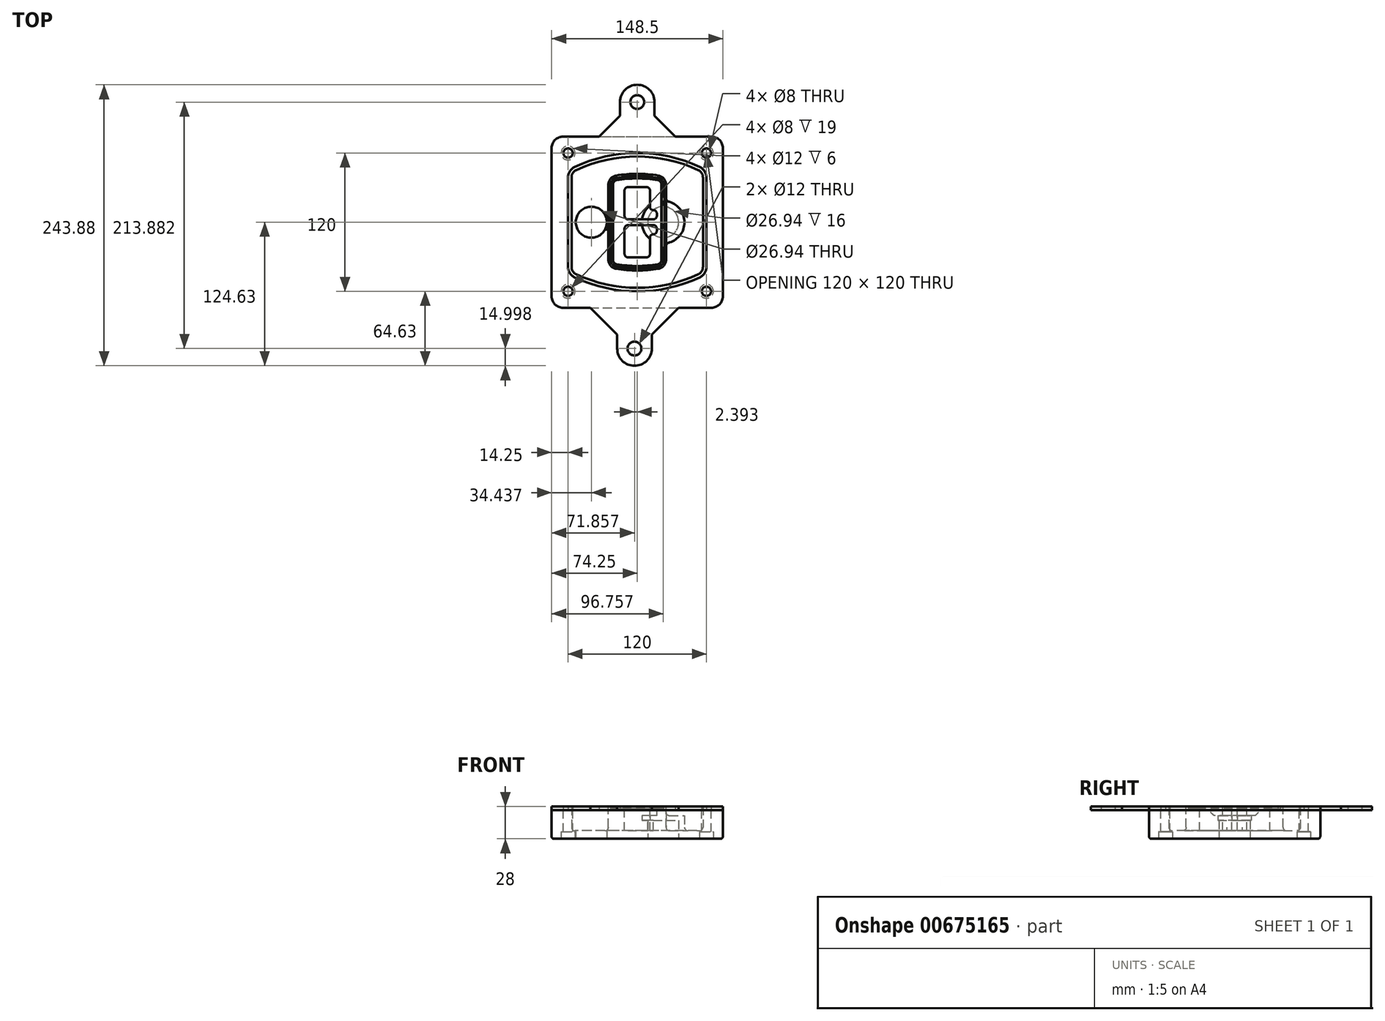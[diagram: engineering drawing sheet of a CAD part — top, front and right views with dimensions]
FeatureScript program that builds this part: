
annotation { "Feature Type Name" : "Feature", "Feature Type Description" : "" }
export const myFeature = defineFeature(function(context is Context, id is Id, definition is map)
    precondition{}
    {
        {
            var Q0;
            Q0=qCreatedBy(makeId("Top.planeOp"),FACE);
            var sketch = newSketch(context, id + "F0", { "sketchPlane" : qUnion([Q0])});
            skPoint(sketch, "E0.rect.middle", {"position": v(0, 0) * mm});
            skLineSegment(sketch, "E1.bottom", {"start": v(-64.25, -74.25) * mm, "end": v(64.25, -74.25) * mm});
            skLineSegment(sketch, "E1.top", {"start": v(-64.25, 74.25) * mm, "end": v(64.25, 74.25) * mm});
            skLineSegment(sketch, "E1.left", {"start": v(-74.25, -64.25) * mm, "end": v(-74.25, 64.25) * mm});
            skLineSegment(sketch, "E1.right", {"start": v(74.25, -64.25) * mm, "end": v(74.25, 64.25) * mm});
            skLineSegment(sketch, "E2", {"start": v(-74.25, 74.25) * mm, "end": v(74.25, -74.25) * mm, "construction": true});
            skLineSegment(sketch, "E3", {"start": v(74.25, 74.25) * mm, "end": v(-74.25, -74.25) * mm, "construction": true});
            skCircle(sketch, "E4", {"center": v(-60, 60) * mm, "radius": 4 * mm});
            skCircle(sketch, "E5", {"center": v(60, 60) * mm, "radius": 4 * mm});
            skCircle(sketch, "E6", {"center": v(60, -60) * mm, "radius": 4 * mm});
            skCircle(sketch, "E7", {"center": v(-60, -60) * mm, "radius": 4 * mm});
            skLineSegment(sketch, "E8", {"start": v(-60, 60) * mm, "end": v(60, 60) * mm, "construction": true});
            skLineSegment(sketch, "E9", {"start": v(60, 60) * mm, "end": v(60, -60) * mm, "construction": true});
            skLineSegment(sketch, "E10", {"start": v(60, -60) * mm, "end": v(-60, -60) * mm, "construction": true});
            skLineSegment(sketch, "E11", {"start": v(-60, -60) * mm, "end": v(-60, 60) * mm, "construction": true});
            skLineSegment(sketch, "E12", {"start": v(-60, 38.83) * mm, "end": v(-60, -38.83) * mm});
            skLineSegment(sketch, "E13", {"start": v(60, 38.83) * mm, "end": v(60, -38.83) * mm});
            skArc(sketch, "E14", {"start": v(54.26, 47.88) * mm, "mid": v(0, 60) * mm, "end": v(-54.26, 47.88) * mm});
            skArc(sketch, "E15", {"start": v(-54.26, -47.88) * mm, "mid": v(0, -60) * mm, "end": v(54.26, -47.88) * mm});
            skLineSegment(sketch, "E16", {"start": v(-60, 0) * mm, "end": v(60, 0) * mm, "construction": true});
            skPoint(sketch, "E17.visualSharp", {"position": v(-60, -45) * mm});
            skArc(sketch, "E17.filletArc", {"start": v(-60, -38.83) * mm, "mid": v(-58.44, -44.2) * mm, "end": v(-54.26, -47.88) * mm});
            skPoint(sketch, "E18.visualSharp", {"position": v(-60, 45) * mm});
            skArc(sketch, "E18.filletArc", {"start": v(-54.26, 47.88) * mm, "mid": v(-58.44, 44.2) * mm, "end": v(-60, 38.83) * mm});
            skPoint(sketch, "E19.visualSharp", {"position": v(60, 45) * mm});
            skArc(sketch, "E19.filletArc", {"start": v(60, 38.83) * mm, "mid": v(58.44, 44.2) * mm, "end": v(54.26, 47.88) * mm});
            skPoint(sketch, "E20.visualSharp", {"position": v(60, -45) * mm});
            skArc(sketch, "E20.filletArc", {"start": v(54.26, -47.88) * mm, "mid": v(58.44, -44.2) * mm, "end": v(60, -38.83) * mm});
            skPoint(sketch, "E21.visualSharp", {"position": v(-74.25, 74.25) * mm});
            skArc(sketch, "E21.filletArc", {"start": v(-64.25, 74.25) * mm, "mid": v(-71.32, 71.32) * mm, "end": v(-74.25, 64.25) * mm});
            skPoint(sketch, "E22.visualSharp", {"position": v(74.25, 74.25) * mm});
            skArc(sketch, "E22.filletArc", {"start": v(74.25, 64.25) * mm, "mid": v(71.32, 71.32) * mm, "end": v(64.25, 74.25) * mm});
            skPoint(sketch, "E23.visualSharp", {"position": v(74.25, -74.25) * mm});
            skArc(sketch, "E23.filletArc", {"start": v(64.25, -74.25) * mm, "mid": v(71.32, -71.32) * mm, "end": v(74.25, -64.25) * mm});
            skPoint(sketch, "E24.visualSharp", {"position": v(-74.25, -74.25) * mm});
            skArc(sketch, "E24.filletArc", {"start": v(-74.25, -64.25) * mm, "mid": v(-71.32, -71.32) * mm, "end": v(-64.25, -74.25) * mm});
            skArc(sketch, "E25.0", {"start": v(57, 38.83) * mm, "mid": v(55.9, 42.58) * mm, "end": v(52.98, 45.17) * mm});
            skLineSegment(sketch, "E25.1", {"start": v(57, 38.83) * mm, "end": v(57, -38.83) * mm});
            skArc(sketch, "E25.2", {"start": v(52.98, -45.17) * mm, "mid": v(55.9, -42.58) * mm, "end": v(57, -38.83) * mm});
            skArc(sketch, "E25.3", {"start": v(-52.98, -45.17) * mm, "mid": v(0, -57) * mm, "end": v(52.98, -45.17) * mm});
            skArc(sketch, "E25.4", {"start": v(-57, -38.83) * mm, "mid": v(-55.9, -42.58) * mm, "end": v(-52.98, -45.17) * mm});
            skArc(sketch, "E25.5", {"start": v(52.98, 45.17) * mm, "mid": v(0, 57) * mm, "end": v(-52.98, 45.17) * mm});
            skLineSegment(sketch, "E25.6", {"start": v(-57, 38.83) * mm, "end": v(-57, -38.83) * mm});
            skArc(sketch, "E25.7", {"start": v(-52.98, 45.17) * mm, "mid": v(-55.9, 42.58) * mm, "end": v(-57, 38.83) * mm});
            skArc(sketch, "E26.0", {"start": v(-55.96, 51.5) * mm, "mid": v(-61.82, 46.33) * mm, "end": v(-64, 38.83) * mm});
            skArc(sketch, "E26.1", {"start": v(55.96, 51.5) * mm, "mid": v(0, 64) * mm, "end": v(-55.96, 51.5) * mm});
            skArc(sketch, "E26.2", {"start": v(64, 38.83) * mm, "mid": v(61.82, 46.33) * mm, "end": v(55.96, 51.5) * mm});
            skLineSegment(sketch, "E26.3", {"start": v(64, 38.83) * mm, "end": v(64, -38.83) * mm});
            skArc(sketch, "E26.4", {"start": v(55.96, -51.5) * mm, "mid": v(61.82, -46.33) * mm, "end": v(64, -38.83) * mm});
            skLineSegment(sketch, "E26.5", {"start": v(-64, 38.83) * mm, "end": v(-64, -38.83) * mm});
            skArc(sketch, "E26.6", {"start": v(-55.96, -51.5) * mm, "mid": v(0, -64) * mm, "end": v(55.96, -51.5) * mm});
            skArc(sketch, "E26.7", {"start": v(-64, -38.83) * mm, "mid": v(-61.82, -46.33) * mm, "end": v(-55.96, -51.5) * mm});
            skPoint(sketch, "E27.startSnap0", {"position": v(0, 74.25) * mm});
            skCircle(sketch, "E28", {"center": v(0, 104.25) * mm, "radius": 6 * mm});
            skArc(sketch, "E29", {"start": v(-15, 104.25) * mm, "mid": v(0, 119.25) * mm, "end": v(15, 104.25) * mm});
            skLineSegment(sketch, "E30", {"start": v(-15, 104.25) * mm, "end": v(-15, 92.25) * mm});
            skLineSegment(sketch, "E31", {"start": v(15, 104.25) * mm, "end": v(15, 92.25) * mm});
            skLineSegment(sketch, "E32", {"start": v(-15, 92.25) * mm, "end": v(-33, 74.25) * mm});
            skLineSegment(sketch, "E33", {"start": v(15, 92.25) * mm, "end": v(33, 74.25) * mm});
            skCircle(sketch, "E34", {"center": v(-2.4, -109.63) * mm, "radius": 6 * mm});
            skArc(sketch, "E35", {"start": v(-17.4, -109.63) * mm, "mid": v(-2.4, -124.63) * mm, "end": v(12.6, -109.63) * mm});
            skLineSegment(sketch, "E36", {"start": v(12.6, -109.63) * mm, "end": v(12.6, -97.63) * mm});
            skLineSegment(sketch, "E37", {"start": v(-17.4, -109.63) * mm, "end": v(-17.4, -97.63) * mm});
            skLineSegment(sketch, "E38", {"start": v(12.6, -97.63) * mm, "end": v(35.99, -74.25) * mm});
            skLineSegment(sketch, "E39", {"start": v(-17.4, -97.63) * mm, "end": v(-40.77, -74.25) * mm});
            skSolve(sketch);
        }
        {
            var Q0;
            Q0=makeQuery(id+"F0.imprint","IMPRINT",FACE,{"disambiguationData":[TD([[makeQuery(id+"F0.imprint","IMPRINT",EDGE,{"derivedFrom":sQuery(id+"F0.wireOp",EDGE,"E1.bottom")}),1.0]])]});
            var Q1;
            Q1=makeQuery(id+"F0.imprint","IMPRINT",FACE,{"disambiguationData":[TD([[makeQuery(id+"F0.imprint","IMPRINT",EDGE,{"derivedFrom":sQuery(id+"F0.wireOp",EDGE,"E12")}),1.0]])]});
            var Q2;
            Q2=makeQuery(id+"F0.imprint","IMPRINT",FACE,{"disambiguationData":[TD([[makeQuery(id+"F0.imprint","IMPRINT",EDGE,{"derivedFrom":sQuery(id+"F0.wireOp",EDGE,"E25.0")}),1.0]])]});
            var Q3;
            Q3=makeQuery(id+"F0.imprint","IMPRINT",FACE,{"disambiguationData":[TD([[makeQuery(id+"F0.imprint","IMPRINT",EDGE,{"derivedFrom":sQuery(id+"F0.wireOp",EDGE,"E12")}),-1.0]])]});
            extrude(context, id + "F1", {"entities" : qUnion([Q0, Q1, Q2, Q3]), "oppositeDirection" : true, "depth" : 25 * mm});
        }
        {
            var Q0;
            Q0=makeQuery(id+"F0.imprint","IMPRINT",FACE,{"disambiguationData":[TD([[makeQuery(id+"F0.imprint","IMPRINT",EDGE,{"derivedFrom":sQuery(id+"F0.wireOp",EDGE,"E12")}),1.0]])]});
            extrude(context, id + "F2", {"entities" : qUnion([Q0]), "operationType" : NewBodyOperationType.ADD, "depth" : 3 * mm});
        }
        {
            var Q0;
            Q0=makeQuery(id+"F0.imprint","IMPRINT",FACE,{"disambiguationData":[TD([[makeQuery(id+"F0.imprint","IMPRINT",EDGE,{"derivedFrom":sQuery(id+"F0.wireOp",EDGE,"E25.0")}),1.0]])]});
            extrude(context, id + "F3", {"entities" : qUnion([Q0]), "operationType" : NewBodyOperationType.REMOVE, "oppositeDirection" : true, "depth" : 18 * mm});
        }
        {
            var Q0;
            Q0=makeQuery(id+"F2.opExtrude","CAP_FACE",FACE,{"disambiguationData":[OSD([sQuery(id+"F0.wireOp",EDGE,"E12"),sQuery(id+"F0.wireOp",EDGE,"E13"),sQuery(id+"F0.wireOp",EDGE,"E14"),sQuery(id+"F0.wireOp",EDGE,"E15"),sQuery(id+"F0.wireOp",EDGE,"E17.filletArc"),sQuery(id+"F0.wireOp",EDGE,"E18.filletArc"),sQuery(id+"F0.wireOp",EDGE,"E19.filletArc"),sQuery(id+"F0.wireOp",EDGE,"E20.filletArc"),sQuery(id+"F0.wireOp",EDGE,"E25.0"),sQuery(id+"F0.wireOp",EDGE,"E25.1"),sQuery(id+"F0.wireOp",EDGE,"E25.2"),sQuery(id+"F0.wireOp",EDGE,"E25.3"),sQuery(id+"F0.wireOp",EDGE,"E25.4"),sQuery(id+"F0.wireOp",EDGE,"E25.5"),sQuery(id+"F0.wireOp",EDGE,"E25.6"),sQuery(id+"F0.wireOp",EDGE,"E25.7")])],"isStart":false});
            var sketch = newSketch(context, id + "F4", { "sketchPlane" : qUnion([Q0])});
            skArc(sketch, "E40.0", {"start": v(-18.34, -40.45) * mm, "mid": v(0, -42) * mm, "end": v(18.34, -40.45) * mm});
            skArc(sketch, "E41.0", {"start": v(18.34, 40.45) * mm, "mid": v(0, 42) * mm, "end": v(-18.34, 40.45) * mm});
            skLineSegment(sketch, "E42", {"start": v(-25, 32.57) * mm, "end": v(-25, -32.57) * mm});
            skLineSegment(sketch, "E43", {"start": v(25, 32.57) * mm, "end": v(25, -32.57) * mm});
            skLineSegment(sketch, "E44", {"start": v(-25, 39.1) * mm, "end": v(25, 39.1) * mm, "construction": true});
            skLineSegment(sketch, "E45", {"start": v(-25, -39.1) * mm, "end": v(25, -39.1) * mm, "construction": true});
            skPoint(sketch, "E46.visualSharp", {"position": v(-25, 39.1) * mm});
            skArc(sketch, "E46.filletArc", {"start": v(-18.34, 40.45) * mm, "mid": v(-23.11, 37.73) * mm, "end": v(-25, 32.57) * mm});
            skPoint(sketch, "E47.visualSharp", {"position": v(25, 39.1) * mm});
            skArc(sketch, "E47.filletArc", {"start": v(25, 32.57) * mm, "mid": v(23.11, 37.73) * mm, "end": v(18.34, 40.45) * mm});
            skPoint(sketch, "E48.visualSharp", {"position": v(25, -39.1) * mm});
            skArc(sketch, "E48.filletArc", {"start": v(18.34, -40.45) * mm, "mid": v(23.11, -37.73) * mm, "end": v(25, -32.57) * mm});
            skPoint(sketch, "E49.visualSharp", {"position": v(-25, -39.1) * mm});
            skArc(sketch, "E49.filletArc", {"start": v(-25, -32.57) * mm, "mid": v(-23.11, -37.73) * mm, "end": v(-18.34, -40.45) * mm});
            skArc(sketch, "E50.0", {"start": v(52.98, 45.17) * mm, "mid": v(0, 57) * mm, "end": v(-52.98, 45.17) * mm});
            skArc(sketch, "E50.1", {"start": v(-52.98, 45.17) * mm, "mid": v(-55.9, 42.58) * mm, "end": v(-57, 38.83) * mm});
            skLineSegment(sketch, "E50.2", {"start": v(-57, 38.83) * mm, "end": v(-57, -38.83) * mm});
            skArc(sketch, "E50.3", {"start": v(-57, -38.83) * mm, "mid": v(-55.9, -42.58) * mm, "end": v(-52.98, -45.17) * mm});
            skArc(sketch, "E50.4", {"start": v(-52.98, -45.17) * mm, "mid": v(0, -57) * mm, "end": v(52.98, -45.17) * mm});
            skArc(sketch, "E50.5", {"start": v(52.98, -45.17) * mm, "mid": v(55.9, -42.58) * mm, "end": v(57, -38.83) * mm});
            skLineSegment(sketch, "E50.6", {"start": v(57, 38.83) * mm, "end": v(57, -38.83) * mm});
            skArc(sketch, "E50.7", {"start": v(57, 38.83) * mm, "mid": v(55.9, 42.58) * mm, "end": v(52.98, 45.17) * mm});
            skLineSegment(sketch, "E51.0", {"start": v(23, 32.57) * mm, "end": v(23, -32.57) * mm});
            skArc(sketch, "E51.1", {"start": v(18, -38.48) * mm, "mid": v(21.58, -36.44) * mm, "end": v(23, -32.57) * mm});
            skArc(sketch, "E51.2", {"start": v(-18, -38.48) * mm, "mid": v(0, -40) * mm, "end": v(18, -38.48) * mm});
            skArc(sketch, "E51.3", {"start": v(-23, -32.57) * mm, "mid": v(-21.58, -36.44) * mm, "end": v(-18, -38.48) * mm});
            skLineSegment(sketch, "E51.4", {"start": v(-23, 32.57) * mm, "end": v(-23, -32.57) * mm});
            skArc(sketch, "E51.5", {"start": v(23, 32.57) * mm, "mid": v(21.58, 36.44) * mm, "end": v(18, 38.48) * mm});
            skArc(sketch, "E51.6", {"start": v(-18, 38.48) * mm, "mid": v(-21.58, 36.44) * mm, "end": v(-23, 32.57) * mm});
            skArc(sketch, "E51.7", {"start": v(18, 38.48) * mm, "mid": v(0, 40) * mm, "end": v(-18, 38.48) * mm});
            skArc(sketch, "E52.0", {"start": v(21, 32.57) * mm, "mid": v(20.06, 35.15) * mm, "end": v(17.67, 36.5) * mm});
            skLineSegment(sketch, "E52.1", {"start": v(21, 32.57) * mm, "end": v(21, -32.57) * mm});
            skArc(sketch, "E52.2", {"start": v(17.67, -36.5) * mm, "mid": v(20.06, -35.15) * mm, "end": v(21, -32.57) * mm});
            skArc(sketch, "E52.3", {"start": v(-17.67, -36.5) * mm, "mid": v(0, -38) * mm, "end": v(17.67, -36.5) * mm});
            skArc(sketch, "E52.4", {"start": v(-21, -32.57) * mm, "mid": v(-20.06, -35.15) * mm, "end": v(-17.67, -36.5) * mm});
            skArc(sketch, "E52.5", {"start": v(17.67, 36.5) * mm, "mid": v(0, 38) * mm, "end": v(-17.67, 36.5) * mm});
            skLineSegment(sketch, "E52.6", {"start": v(-21, 32.57) * mm, "end": v(-21, -32.57) * mm});
            skArc(sketch, "E52.7", {"start": v(-17.67, 36.5) * mm, "mid": v(-20.06, 35.15) * mm, "end": v(-21, 32.57) * mm});
            skLineSegment(sketch, "E53", {"start": v(-25, 0) * mm, "end": v(25, 0) * mm, "construction": true});
            skLineSegment(sketch, "E54", {"start": v(-11, 5.5) * mm, "end": v(-11, 27.5) * mm});
            skLineSegment(sketch, "E55", {"start": v(-8, 30.5) * mm, "end": v(8, 30.5) * mm});
            skLineSegment(sketch, "E56", {"start": v(11, 27.5) * mm, "end": v(11, 13.5) * mm});
            skLineSegment(sketch, "E57", {"start": v(14, 10.5) * mm, "end": v(14, 10.5) * mm});
            skLineSegment(sketch, "E58", {"start": v(17, 7.5) * mm, "end": v(17, 5.5) * mm});
            skLineSegment(sketch, "E59", {"start": v(14, 2.5) * mm, "end": v(-8, 2.5) * mm});
            skPoint(sketch, "E60.visualSharp", {"position": v(-11, 30.5) * mm});
            skArc(sketch, "E60.filletArc", {"start": v(-8, 30.5) * mm, "mid": v(-10.12, 29.62) * mm, "end": v(-11, 27.5) * mm});
            skPoint(sketch, "E61.visualSharp", {"position": v(11, 30.5) * mm});
            skArc(sketch, "E61.filletArc", {"start": v(11, 27.5) * mm, "mid": v(10.12, 29.62) * mm, "end": v(8, 30.5) * mm});
            skPoint(sketch, "E62.visualSharp", {"position": v(11, 10.5) * mm});
            skArc(sketch, "E62.filletArc", {"start": v(11, 13.5) * mm, "mid": v(11.88, 11.38) * mm, "end": v(14, 10.5) * mm});
            skPoint(sketch, "E63.visualSharp", {"position": v(17, 10.5) * mm});
            skArc(sketch, "E63.filletArc", {"start": v(17, 7.5) * mm, "mid": v(16.12, 9.62) * mm, "end": v(14, 10.5) * mm});
            skPoint(sketch, "E64.visualSharp", {"position": v(17, 2.5) * mm});
            skArc(sketch, "E64.filletArc", {"start": v(14, 2.5) * mm, "mid": v(16.12, 3.38) * mm, "end": v(17, 5.5) * mm});
            skPoint(sketch, "E65.visualSharp", {"position": v(-11, 2.5) * mm});
            skArc(sketch, "E65.filletArc", {"start": v(-11, 5.5) * mm, "mid": v(-10.12, 3.38) * mm, "end": v(-8, 2.5) * mm});
            skLineSegment(sketch, "E66.0.MirrorCS", {"start": v(14, -2.5) * mm, "end": v(-8, -2.5) * mm});
            skArc(sketch, "E67.0.MirrorCS", {"start": v(-11, -5.5) * mm, "mid": v(-10.12, -3.38) * mm, "end": v(-8, -2.5) * mm});
            skLineSegment(sketch, "E68.0.MirrorCS", {"start": v(-11, -5.5) * mm, "end": v(-11, -27.5) * mm});
            skArc(sketch, "E69.0.MirrorCS", {"start": v(-8, -30.5) * mm, "mid": v(-10.12, -29.62) * mm, "end": v(-11, -27.5) * mm});
            skLineSegment(sketch, "E70.0.MirrorCS", {"start": v(-8, -30.5) * mm, "end": v(8, -30.5) * mm});
            skArc(sketch, "E71.0.MirrorCS", {"start": v(11, -27.5) * mm, "mid": v(10.12, -29.62) * mm, "end": v(8, -30.5) * mm});
            skLineSegment(sketch, "E72.0.MirrorCS", {"start": v(11, -27.5) * mm, "end": v(11, -13.5) * mm});
            skArc(sketch, "E73.0.MirrorCS", {"start": v(11, -13.5) * mm, "mid": v(11.88, -11.38) * mm, "end": v(14, -10.5) * mm});
            skArc(sketch, "E74.0.MirrorCS", {"start": v(17, -7.5) * mm, "mid": v(16.12, -9.62) * mm, "end": v(14, -10.5) * mm});
            skLineSegment(sketch, "E75.0.MirrorCS", {"start": v(17, -7.5) * mm, "end": v(17, -5.5) * mm});
            skArc(sketch, "E76.0.MirrorCS", {"start": v(14, -2.5) * mm, "mid": v(16.12, -3.38) * mm, "end": v(17, -5.5) * mm});
            skSolve(sketch);
        }
        {
            var Q0;
            Q0=makeQuery(id+"F4.imprint","IMPRINT",FACE,{"disambiguationData":[TD([[makeQuery(id+"F4.imprint","IMPRINT",EDGE,{"derivedFrom":sQuery(id+"F4.wireOp",EDGE,"E40.0")}),1.0]])]});
            var Q1;
            Q1=makeQuery(id+"F4.imprint","IMPRINT",FACE,{"disambiguationData":[TD([[makeQuery(id+"F4.imprint","IMPRINT",EDGE,{"derivedFrom":sQuery(id+"F4.wireOp",EDGE,"E51.0")}),-1.0]])]});
            var Q2;
            Q2=makeQuery(id+"F4.imprint","IMPRINT",FACE,{"disambiguationData":[TD([[makeQuery(id+"F4.imprint","IMPRINT",EDGE,{"derivedFrom":sQuery(id+"F4.wireOp",EDGE,"E52.0")}),1.0]])]});
            extrude(context, id + "F5", {"entities" : qUnion([Q0, Q1, Q2]), "operationType" : NewBodyOperationType.ADD, "endBound" : BoundingType.UP_TO_NEXT, "oppositeDirection" : true, "depth" : 25 * mm});
        }
        {
            var Q0;
            Q0=makeQuery(id+"F4.imprint","IMPRINT",FACE,{"disambiguationData":[TD([[makeQuery(id+"F4.imprint","IMPRINT",EDGE,{"derivedFrom":sQuery(id+"F4.wireOp",EDGE,"E51.0")}),-1.0]])]});
            extrude(context, id + "F6", {"entities" : qUnion([Q0]), "operationType" : NewBodyOperationType.REMOVE, "oppositeDirection" : true, "depth" : 2 * mm});
        }
        {
            var Q0;
            Q0=makeQuery(id+"F1.opExtrude","CAP_FACE",FACE,{"disambiguationData":[OSD([sQuery(id+"F0.wireOp",EDGE,"E1.bottom"),sQuery(id+"F0.wireOp",EDGE,"E1.top"),sQuery(id+"F0.wireOp",EDGE,"E1.left"),sQuery(id+"F0.wireOp",EDGE,"E1.right"),sQuery(id+"F0.wireOp",EDGE,"E4"),sQuery(id+"F0.wireOp",EDGE,"E5"),sQuery(id+"F0.wireOp",EDGE,"E6"),sQuery(id+"F0.wireOp",EDGE,"E7"),sQuery(id+"F0.wireOp",EDGE,"E21.filletArc"),sQuery(id+"F0.wireOp",EDGE,"E22.filletArc"),sQuery(id+"F0.wireOp",EDGE,"E23.filletArc"),sQuery(id+"F0.wireOp",EDGE,"E24.filletArc")])],"isStart":false});
            var sketch = newSketch(context, id + "F7", { "sketchPlane" : qUnion([Q0])});
            skCircle(sketch, "E77", {"center": v(22.5, 0) * mm, "radius": 13.47 * mm});
            skCircle(sketch, "E78", {"center": v(-39.81, 0) * mm, "radius": 13.47 * mm});
            skLineSegment(sketch, "E79", {"start": v(74.25, 0) * mm, "end": v(-74.25, 0) * mm});
            skCircle(sketch, "E80", {"center": v(22.5, 0) * mm, "radius": 18.47 * mm});
            skCircle(sketch, "E81", {"center": v(60, -60) * mm, "radius": 6 * mm});
            skCircle(sketch, "E82", {"center": v(-60, -60) * mm, "radius": 6 * mm});
            skCircle(sketch, "E83", {"center": v(-60, 60) * mm, "radius": 6 * mm});
            skCircle(sketch, "E84", {"center": v(60, 60) * mm, "radius": 6 * mm});
            skSolve(sketch);
        }
        {
            var Q0;
            {var subQ1=sQuery(id+"F7.wireOp",EDGE,"E79");var subQ4=sQuery(id+"F7.wireOp",EDGE,"E77");var subQ6=makeQuery(id+"F7.imprint","INTERSECT",VERTEX,{"disambiguationData":[OD(0.0)],"derivedFrom":[subQ4,subQ1]});Q0=makeQuery(id+"F7.imprint","IMPRINT",FACE,{"disambiguationData":[TD([[makeQuery(id+"F7.imprint","IMPRINT",EDGE,{"disambiguationData":[TD([[subQ6,-1.0]])],"derivedFrom":subQ4}),-1.0]])]});}
            var Q1;
            {var subQ0=sQuery(id+"F7.wireOp",EDGE,"E79");var subQ1=sQuery(id+"F7.wireOp",EDGE,"E77");var subQ3=makeQuery(id+"F7.imprint","INTERSECT",VERTEX,{"disambiguationData":[OD(0.0)],"derivedFrom":[subQ1,subQ0]});Q1=makeQuery(id+"F7.imprint","IMPRINT",FACE,{"disambiguationData":[TD([[makeQuery(id+"F7.imprint","IMPRINT",EDGE,{"disambiguationData":[TD([[subQ3,-1.0]])],"derivedFrom":subQ1}),1.0]])]});}
            var Q2;
            {var subQ0=sQuery(id+"F7.wireOp",EDGE,"E79");var subQ1=sQuery(id+"F7.wireOp",EDGE,"E77");var subQ3=makeQuery(id+"F7.imprint","INTERSECT",VERTEX,{"disambiguationData":[OD(0.0)],"derivedFrom":[subQ1,subQ0]});Q2=makeQuery(id+"F7.imprint","IMPRINT",FACE,{"disambiguationData":[TD([[makeQuery(id+"F7.imprint","IMPRINT",EDGE,{"disambiguationData":[TD([[subQ3,1.0]])],"derivedFrom":subQ1}),1.0]])]});}
            var Q3;
            {var subQ1=sQuery(id+"F7.wireOp",EDGE,"E79");var subQ4=sQuery(id+"F7.wireOp",EDGE,"E77");var subQ6=makeQuery(id+"F7.imprint","INTERSECT",VERTEX,{"disambiguationData":[OD(0.0)],"derivedFrom":[subQ4,subQ1]});Q3=makeQuery(id+"F7.imprint","IMPRINT",FACE,{"disambiguationData":[TD([[makeQuery(id+"F7.imprint","IMPRINT",EDGE,{"disambiguationData":[TD([[subQ6,1.0]])],"derivedFrom":subQ4}),-1.0]])]});}
            extrude(context, id + "F8", {"entities" : qUnion([Q0, Q1, Q2, Q3]), "operationType" : NewBodyOperationType.ADD, "oppositeDirection" : true, "depth" : 20 * mm});
        }
        {
            var Q0;
            {var subQ0=sQuery(id+"F7.wireOp",EDGE,"E79");var subQ1=sQuery(id+"F7.wireOp",EDGE,"E77");var subQ3=makeQuery(id+"F7.imprint","INTERSECT",VERTEX,{"disambiguationData":[OD(0.0)],"derivedFrom":[subQ1,subQ0]});Q0=makeQuery(id+"F7.imprint","IMPRINT",FACE,{"disambiguationData":[TD([[makeQuery(id+"F7.imprint","IMPRINT",EDGE,{"disambiguationData":[TD([[subQ3,-1.0]])],"derivedFrom":subQ1}),1.0]])]});}
            var Q1;
            {var subQ0=sQuery(id+"F7.wireOp",EDGE,"E79");var subQ1=sQuery(id+"F7.wireOp",EDGE,"E77");var subQ3=makeQuery(id+"F7.imprint","INTERSECT",VERTEX,{"disambiguationData":[OD(0.0)],"derivedFrom":[subQ1,subQ0]});Q1=makeQuery(id+"F7.imprint","IMPRINT",FACE,{"disambiguationData":[TD([[makeQuery(id+"F7.imprint","IMPRINT",EDGE,{"disambiguationData":[TD([[subQ3,1.0]])],"derivedFrom":subQ1}),1.0]])]});}
            extrude(context, id + "F9", {"entities" : qUnion([Q0, Q1]), "operationType" : NewBodyOperationType.REMOVE, "oppositeDirection" : true, "depth" : 16 * mm});
        }
        {
            var Q0;
            {var subQ0=sQuery(id+"F7.wireOp",EDGE,"E79");var subQ1=sQuery(id+"F7.wireOp",EDGE,"E78");var subQ3=makeQuery(id+"F7.imprint","INTERSECT",VERTEX,{"disambiguationData":[OD(0.0)],"derivedFrom":[subQ1,subQ0]});Q0=makeQuery(id+"F7.imprint","IMPRINT",FACE,{"disambiguationData":[TD([[makeQuery(id+"F7.imprint","IMPRINT",EDGE,{"disambiguationData":[TD([[subQ3,-1.0]])],"derivedFrom":subQ1}),1.0]])]});}
            var Q1;
            {var subQ0=sQuery(id+"F7.wireOp",EDGE,"E79");var subQ1=sQuery(id+"F7.wireOp",EDGE,"E78");var subQ3=makeQuery(id+"F7.imprint","INTERSECT",VERTEX,{"disambiguationData":[OD(0.0)],"derivedFrom":[subQ1,subQ0]});Q1=makeQuery(id+"F7.imprint","IMPRINT",FACE,{"disambiguationData":[TD([[makeQuery(id+"F7.imprint","IMPRINT",EDGE,{"disambiguationData":[TD([[subQ3,1.0]])],"derivedFrom":subQ1}),1.0]])]});}
            extrude(context, id + "F10", {"entities" : qUnion([Q0, Q1]), "operationType" : NewBodyOperationType.REMOVE, "oppositeDirection" : true, "depth" : 25 * mm});
        }
        {
            var Q0;
            Q0=makeQuery(id+"F7.imprint","IMPRINT",FACE,{"disambiguationData":[TD([[makeQuery(id+"F7.imprint","IMPRINT",EDGE,{"derivedFrom":sQuery(id+"F7.wireOp",EDGE,"E81")}),1.0]])]});
            var Q1;
            Q1=makeQuery(id+"F7.imprint","IMPRINT",FACE,{"disambiguationData":[TD([[makeQuery(id+"F7.imprint","IMPRINT",EDGE,{"derivedFrom":makeQuery(id+"F1.opExtrude","CAP_EDGE",EDGE,{"disambiguationData":[OSD([sQuery(id+"F0.wireOp",EDGE,"E5")])],"isStart":false})}),-1.0]])]});
            var Q2;
            Q2=makeQuery(id+"F7.imprint","IMPRINT",FACE,{"disambiguationData":[TD([[makeQuery(id+"F7.imprint","IMPRINT",EDGE,{"derivedFrom":sQuery(id+"F7.wireOp",EDGE,"E82")}),1.0]])]});
            var Q3;
            Q3=makeQuery(id+"F7.imprint","IMPRINT",FACE,{"disambiguationData":[TD([[makeQuery(id+"F7.imprint","IMPRINT",EDGE,{"derivedFrom":makeQuery(id+"F1.opExtrude","CAP_EDGE",EDGE,{"disambiguationData":[OSD([sQuery(id+"F0.wireOp",EDGE,"E4")])],"isStart":false})}),-1.0]])]});
            var Q4;
            Q4=makeQuery(id+"F7.imprint","IMPRINT",FACE,{"disambiguationData":[TD([[makeQuery(id+"F7.imprint","IMPRINT",EDGE,{"derivedFrom":sQuery(id+"F7.wireOp",EDGE,"E83")}),1.0]])]});
            var Q5;
            Q5=makeQuery(id+"F7.imprint","IMPRINT",FACE,{"disambiguationData":[TD([[makeQuery(id+"F7.imprint","IMPRINT",EDGE,{"derivedFrom":makeQuery(id+"F1.opExtrude","CAP_EDGE",EDGE,{"disambiguationData":[OSD([sQuery(id+"F0.wireOp",EDGE,"E7")])],"isStart":false})}),-1.0]])]});
            var Q6;
            Q6=makeQuery(id+"F7.imprint","IMPRINT",FACE,{"disambiguationData":[TD([[makeQuery(id+"F7.imprint","IMPRINT",EDGE,{"derivedFrom":sQuery(id+"F7.wireOp",EDGE,"E84")}),1.0]])]});
            var Q7;
            Q7=makeQuery(id+"F7.imprint","IMPRINT",FACE,{"disambiguationData":[TD([[makeQuery(id+"F7.imprint","IMPRINT",EDGE,{"derivedFrom":makeQuery(id+"F1.opExtrude","CAP_EDGE",EDGE,{"disambiguationData":[OSD([sQuery(id+"F0.wireOp",EDGE,"E6")])],"isStart":false})}),-1.0]])]});
            extrude(context, id + "F11", {"entities" : qUnion([Q0, Q1, Q2, Q3, Q4, Q5, Q6, Q7]), "operationType" : NewBodyOperationType.REMOVE, "oppositeDirection" : true, "depth" : 6 * mm});
        }
        {
            var Q0;
            Q0=makeQuery(id+"F9.boolean.opBoolean","COPY",FACE,{"derivedFrom":makeQuery(id+"F9.opExtrude","CAP_FACE",FACE,{"disambiguationData":[OSD([sQuery(id+"F7.wireOp",EDGE,"E77")])],"isStart":false})});
            var sketch = newSketch(context, id + "F12", { "sketchPlane" : qUnion([Q0])});
            skArc(sketch, "E85.0", {"start": v(11, 14.45) * mm, "mid": v(6.45, 9.13) * mm, "end": v(4.2, 2.5) * mm});
            skArc(sketch, "E85.1", {"start": v(4.2, -2.5) * mm, "mid": v(6.45, -9.13) * mm, "end": v(11, -14.45) * mm});
            skLineSegment(sketch, "E86", {"start": v(4.2, -2.5) * mm, "end": v(14, -2.5) * mm});
            skLineSegment(sketch, "E87.0", {"start": v(14, 2.5) * mm, "end": v(4.2, 2.5) * mm});
            skArc(sketch, "E87.1", {"start": v(14, 2.5) * mm, "mid": v(16.12, 3.38) * mm, "end": v(17, 5.5) * mm});
            skLineSegment(sketch, "E87.2", {"start": v(17, 7.5) * mm, "end": v(17, 5.5) * mm});
            skArc(sketch, "E87.3", {"start": v(17, 7.5) * mm, "mid": v(16.12, 9.62) * mm, "end": v(14, 10.5) * mm});
            skArc(sketch, "E87.4", {"start": v(11, 13.5) * mm, "mid": v(11.88, 11.38) * mm, "end": v(14, 10.5) * mm});
            skLineSegment(sketch, "E87.5", {"start": v(11, 14.45) * mm, "end": v(11, 13.5) * mm});
            skLineSegment(sketch, "E87.7", {"start": v(14, -2.5) * mm, "end": v(4.2, -2.5) * mm});
            skArc(sketch, "E87.8", {"start": v(14, -2.5) * mm, "mid": v(16.12, -3.38) * mm, "end": v(17, -5.5) * mm});
            skLineSegment(sketch, "E87.9", {"start": v(17, -7.5) * mm, "end": v(17, -5.5) * mm});
            skArc(sketch, "E87.10", {"start": v(17, -7.5) * mm, "mid": v(16.12, -9.62) * mm, "end": v(14, -10.5) * mm});
            skArc(sketch, "E87.11", {"start": v(11, -13.5) * mm, "mid": v(11.88, -11.38) * mm, "end": v(14, -10.5) * mm});
            skLineSegment(sketch, "E87.12", {"start": v(11, -14.45) * mm, "end": v(11, -13.5) * mm});
            skPoint(sketch, "E88.orphan", {"position": v(11, -27.5) * mm});
            skPoint(sketch, "E89.orphan", {"position": v(-8, -2.5) * mm});
            skPoint(sketch, "E90.orphan", {"position": v(-8, 2.5) * mm});
            skPoint(sketch, "E91.orphan", {"position": v(11, 27.5) * mm});
            skSolve(sketch);
        }
        {
            var Q0;
            {var subQ7=sQuery(id+"F12.wireOp",EDGE,"E85.0");var subQ14=sQuery(id+"F12.wireOp",EDGE,"E85.1");var subQ16=sQuery(id+"F12.wireOp",EDGE,"E87.1");var subQ18=sQuery(id+"F12.wireOp",EDGE,"E87.8");Q0=qUnion([makeQuery(id+"F12.imprint","IMPRINT",FACE,{"disambiguationData":[TD([[makeQuery(id+"F12.imprint","IMPRINT",EDGE,{"derivedFrom":subQ7}),1.0]])]}),makeQuery(id+"F12.imprint","IMPRINT",FACE,{"disambiguationData":[TD([[makeQuery(id+"F12.imprint","IMPRINT",EDGE,{"derivedFrom":subQ14}),1.0]])]}),makeQuery(id+"F12.imprint","IMPRINT",FACE,{"disambiguationData":[TD([[makeQuery(id+"F12.imprint","IMPRINT",EDGE,{"derivedFrom":subQ16}),1.0]])]}),makeQuery(id+"F12.imprint","IMPRINT",FACE,{"disambiguationData":[TD([[makeQuery(id+"F12.imprint","IMPRINT",EDGE,{"derivedFrom":subQ18}),-1.0]])]})]);}
            var Q1;
            Q1=makeQuery(id+"F5.boolean.opBoolean","SPLIT",FACE,{"disambiguationData":[TD([makeQuery(id+"F5.opExtrude","SWEPT_FACE",FACE,{"disambiguationData":[OSD([sQuery(id+"F4.wireOp",EDGE,"E54")])]})])],"derivedFrom":makeQuery(id+"F3.boolean.opBoolean","COPY",FACE,{"derivedFrom":makeQuery(id+"F3.opExtrude","CAP_FACE",FACE,{"disambiguationData":[OSD([sQuery(id+"F0.wireOp",EDGE,"E25.0"),sQuery(id+"F0.wireOp",EDGE,"E25.1"),sQuery(id+"F0.wireOp",EDGE,"E25.2"),sQuery(id+"F0.wireOp",EDGE,"E25.3"),sQuery(id+"F0.wireOp",EDGE,"E25.4"),sQuery(id+"F0.wireOp",EDGE,"E25.5"),sQuery(id+"F0.wireOp",EDGE,"E25.6"),sQuery(id+"F0.wireOp",EDGE,"E25.7")])],"isStart":false})})});
            extrude(context, id + "F13", {"entities" : qUnion([Q0]), "operationType" : NewBodyOperationType.REMOVE, "endBound" : BoundingType.UP_TO_SURFACE, "endBoundEntityFace" : qUnion([Q1]), "depth" : 25 * mm});
        }
        {
            var Q0;
            Q0=makeQuery(id+"F3.boolean.opBoolean","COPY",EDGE,{"derivedFrom":makeQuery(id+"F3.opExtrude","CAP_EDGE",EDGE,{"disambiguationData":[OSD([sQuery(id+"F0.wireOp",EDGE,"E25.6")])],"isStart":false})});
            var Q1;
            Q1=makeQuery(id+"F8.boolean.opBoolean","INTERSECT",EDGE,{"derivedFrom":[makeQuery(id+"F5.opExtrude","SWEPT_FACE",FACE,{"disambiguationData":[OSD([sQuery(id+"F4.wireOp",EDGE,"E43")])]}),makeQuery(id+"F8.opExtrude","CAP_FACE",FACE,{"disambiguationData":[OSD([sQuery(id+"F7.wireOp",EDGE,"E80")])],"isStart":false})]});
            var Q2;
            Q2=makeQuery(id+"F8.boolean.opBoolean","INTERSECT",EDGE,{"disambiguationData":[OD(1.0)],"derivedFrom":[makeQuery(id+"F5.opExtrude","SWEPT_FACE",FACE,{"disambiguationData":[OSD([sQuery(id+"F4.wireOp",EDGE,"E43")])]}),makeQuery(id+"F8.opExtrude","SWEPT_FACE",FACE,{"disambiguationData":[OSD([sQuery(id+"F7.wireOp",EDGE,"E80")])]})]});
            var Q3;
            {var subQ0=sQuery(id+"F4.wireOp",EDGE,"E43");Q3=makeQuery(id+"F8.boolean.opBoolean","SPLIT",EDGE,{"disambiguationData":[TD([makeQuery(id+"F5.opExtrude","SWEPT_FACE",FACE,{"disambiguationData":[OSD([sQuery(id+"F4.wireOp",EDGE,"E48.filletArc")])]})])],"derivedFrom":makeQuery(id+"F5.opExtrude","CAP_EDGE",EDGE,{"disambiguationData":[OSD([subQ0])],"isStart":false})});}
            var Q4;
            {var subQ0=sQuery(id+"F0.wireOp",EDGE,"E25.7");var subQ1=sQuery(id+"F0.wireOp",EDGE,"E25.1");var subQ2=sQuery(id+"F0.wireOp",EDGE,"E25.6");var subQ3=sQuery(id+"F0.wireOp",EDGE,"E25.5");var subQ4=sQuery(id+"F0.wireOp",EDGE,"E25.4");var subQ5=sQuery(id+"F0.wireOp",EDGE,"E25.0");var subQ6=sQuery(id+"F0.wireOp",EDGE,"E25.2");var subQ7=sQuery(id+"F0.wireOp",EDGE,"E25.3");Q4=makeQuery(id+"F8.boolean.opBoolean","INTERSECT",EDGE,{"derivedFrom":[makeQuery(id+"F5.boolean.opBoolean","SPLIT",FACE,{"disambiguationData":[TD([makeQuery(id+"F2.opExtrude","SWEPT_FACE",FACE,{"disambiguationData":[OSD([subQ5])]})])],"derivedFrom":makeQuery(id+"F3.boolean.opBoolean","COPY",FACE,{"derivedFrom":makeQuery(id+"F3.opExtrude","CAP_FACE",FACE,{"disambiguationData":[OSD([subQ5,subQ1,subQ6,subQ7,subQ4,subQ3,subQ2,subQ0])],"isStart":false})})}),makeQuery(id+"F8.opExtrude","SWEPT_FACE",FACE,{"disambiguationData":[OSD([sQuery(id+"F7.wireOp",EDGE,"E80")])]})]});}
            var Q5;
            Q5=makeQuery(id+"F8.boolean.opBoolean","INTERSECT",EDGE,{"disambiguationData":[OD(0.0)],"derivedFrom":[makeQuery(id+"F5.opExtrude","SWEPT_FACE",FACE,{"disambiguationData":[OSD([sQuery(id+"F4.wireOp",EDGE,"E43")])]}),makeQuery(id+"F8.opExtrude","SWEPT_FACE",FACE,{"disambiguationData":[OSD([sQuery(id+"F7.wireOp",EDGE,"E80")])]})]});
            fillet(context, id + "F14", {"entities" : qUnion([Q0, Q1, Q2, Q3, Q4, Q5]), "radius" : 3 * mm, "tangentPropagation" : true, "allowEdgeOverflow" : false});
        }
        {
            var Q0;
            Q0=makeQuery(id+"F1.opExtrude","CAP_EDGE",EDGE,{"disambiguationData":[OSD([sQuery(id+"F0.wireOp",EDGE,"E1.bottom")])],"isStart":false});
            fillet(context, id + "F15", {"entities" : qUnion([Q0]), "radius" : 2 * mm, "tangentPropagation" : true, "allowEdgeOverflow" : false});
        }
        {
            var Q0;
            Q0=makeQuery(id+"F0.imprint","IMPRINT",FACE,{"disambiguationData":[TD([[makeQuery(id+"F0.imprint","IMPRINT",EDGE,{"derivedFrom":sQuery(id+"F0.wireOp",EDGE,"E28")}),-1.0]])]});
            var Q1;
            Q1=makeQuery(id+"F0.imprint","IMPRINT",FACE,{"disambiguationData":[TD([[makeQuery(id+"F0.imprint","IMPRINT",EDGE,{"derivedFrom":sQuery(id+"F0.wireOp",EDGE,"E1.left")}),-1.0]])]});
            var Q2;
            Q2=makeQuery(id+"F0.imprint","IMPRINT",FACE,{"disambiguationData":[TD([[makeQuery(id+"F0.imprint","IMPRINT",EDGE,{"derivedFrom":sQuery(id+"F0.wireOp",EDGE,"E34")}),-1.0]])]});
            var Q3;
            Q3=makeQuery(id+"F0.imprint","IMPRINT",FACE,{"disambiguationData":[TD([[makeQuery(id+"F0.imprint","IMPRINT",EDGE,{"derivedFrom":sQuery(id+"F0.wireOp",EDGE,"E12")}),-1.0]])]});
            var Q4;
            Q4=makeQuery(id+"F2.opExtrude","CAP_FACE",FACE,{"disambiguationData":[OSD([sQuery(id+"F0.wireOp",EDGE,"E12"),sQuery(id+"F0.wireOp",EDGE,"E13"),sQuery(id+"F0.wireOp",EDGE,"E14"),sQuery(id+"F0.wireOp",EDGE,"E15"),sQuery(id+"F0.wireOp",EDGE,"E17.filletArc"),sQuery(id+"F0.wireOp",EDGE,"E18.filletArc"),sQuery(id+"F0.wireOp",EDGE,"E19.filletArc"),sQuery(id+"F0.wireOp",EDGE,"E20.filletArc"),sQuery(id+"F0.wireOp",EDGE,"E25.0"),sQuery(id+"F0.wireOp",EDGE,"E25.1"),sQuery(id+"F0.wireOp",EDGE,"E25.2"),sQuery(id+"F0.wireOp",EDGE,"E25.3"),sQuery(id+"F0.wireOp",EDGE,"E25.4"),sQuery(id+"F0.wireOp",EDGE,"E25.5"),sQuery(id+"F0.wireOp",EDGE,"E25.6"),sQuery(id+"F0.wireOp",EDGE,"E25.7")])],"isStart":false});
            extrude(context, id + "F16", {"entities" : qUnion([Q0, Q1, Q2, Q3]), "endBound" : BoundingType.UP_TO_SURFACE, "depth" : 25 * mm, "endBoundEntityFace" : qUnion([Q4]), "offsetDistance" : 25 * mm});
        }
    });
